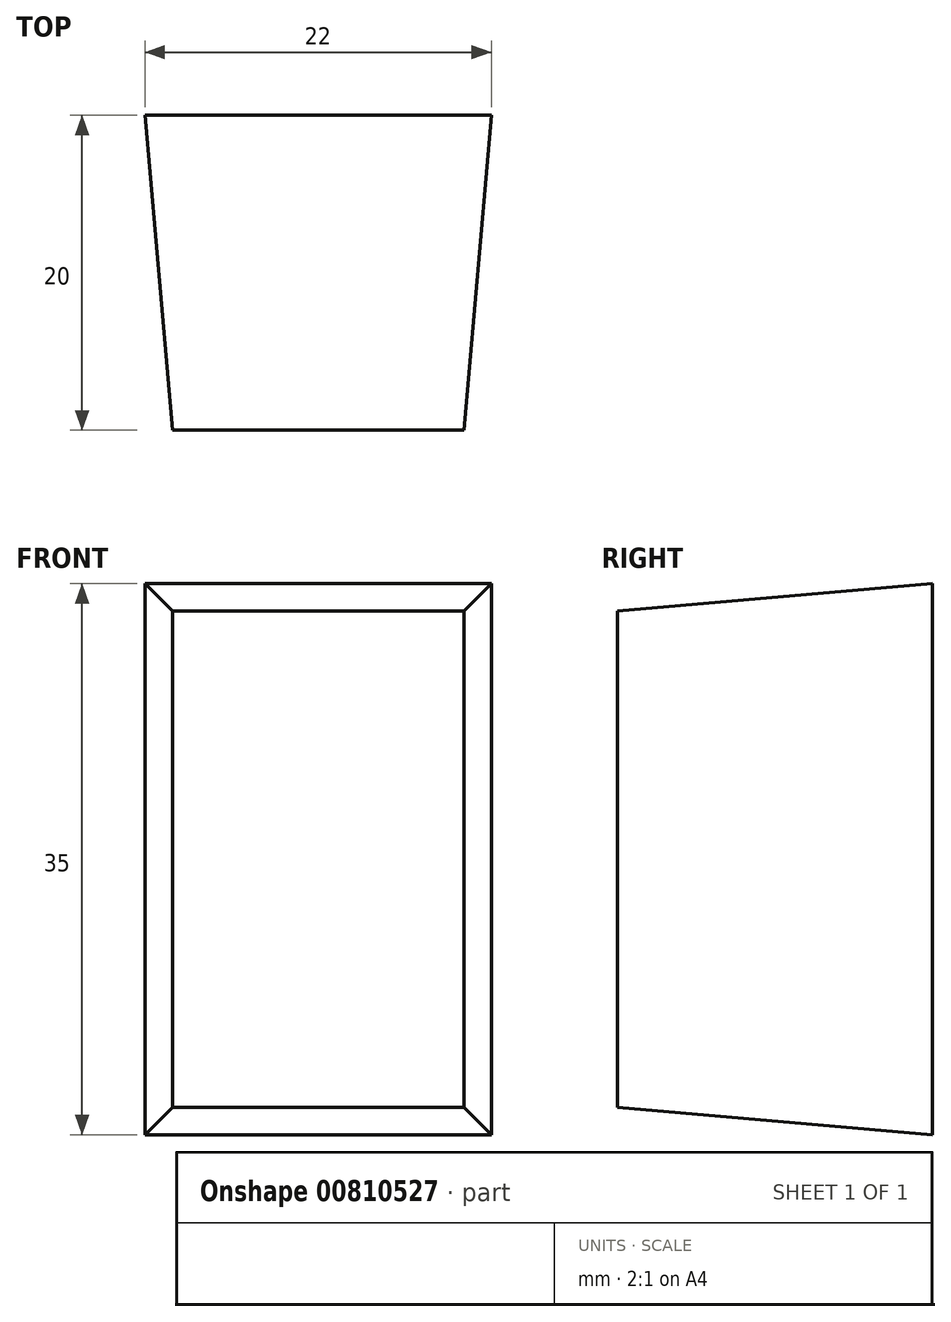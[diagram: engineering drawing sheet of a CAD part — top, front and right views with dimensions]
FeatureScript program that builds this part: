
annotation { "Feature Type Name" : "Feature", "Feature Type Description" : "" }
export const myFeature = defineFeature(function(context is Context, id is Id, definition is map)
    precondition{}
    {
        {
            var Q0;
            Q0=qCreatedBy(makeId("Front.planeOp"),FACE);
            var sketch = newSketch(context, id + "F0", { "sketchPlane" : qUnion([Q0])});
            skLineSegment(sketch, "E0.bottom", {"start": v(11, -17.5) * mm, "end": v(-11, -17.5) * mm});
            skLineSegment(sketch, "E0.top", {"start": v(11, 17.5) * mm, "end": v(-11, 17.5) * mm});
            skLineSegment(sketch, "E0.left", {"start": v(11, -17.5) * mm, "end": v(11, 17.5) * mm});
            skLineSegment(sketch, "E0.right", {"start": v(-11, -17.5) * mm, "end": v(-11, 17.5) * mm});
            skPoint(sketch, "E0.middle", {"position": v(0, 0) * mm});
            skSolve(sketch);
        }
        {
            var Q0;
            Q0=makeQuery(id+"F0.imprint","IMPRINT",FACE,{"disambiguationData":[TD([[makeQuery(id+"F0.imprint","IMPRINT",EDGE,{"derivedFrom":sQuery(id+"F0.wireOp",EDGE,"E0.bottom")}),-1.0]])]});
            extrude(context, id + "F1", {"entities" : qUnion([Q0]), "depth" : 20 * mm, "offsetDistance" : 25 * mm, "hasDraft" : true, "draftAngle" : 5 * degree, "draftPullDirection" : true});
        }
    });
